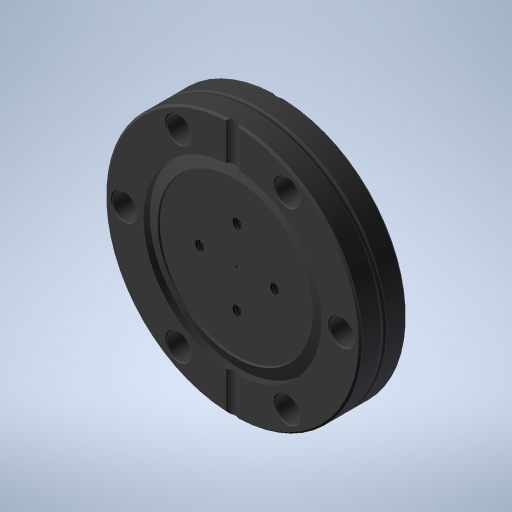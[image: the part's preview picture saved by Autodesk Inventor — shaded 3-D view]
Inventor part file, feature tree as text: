
AUTODESK INVENTOR PART (.ipt)
format: ipt  version: 2024 (Build 280153000, 153)  size: 361,472 bytes
history: native  units: in
note: dims shown in document units (in); Inventor stores cm internally (conversion verified against a paired STEP export)
features: hole x2, sketch x1
ambient origin geometry x8: Origin, YZ Plane, XZ Plane, XY Plane, X Axis, Y Axis, Z Axis, Center Point
bodies: Solid1 (feature_tree)
feature tree (3):
  sketch  "Sketch1"  dims[d0=0.4in d1=0.4in d2=0.4in d3=0.4in d4=0.104in d5=0.25in d6=0.279in d7=0.25in d8=0.5635in d9=0.25in d10=0.0in d11=0.04in d12=0.25in d13=0.375in d14=0.25in d15=0.5635in d16=0.25in d17=0.0in]
  hole  "Hole1"  [1 undecoded]
  hole  "Hole2"  [1 undecoded]
note: 2 required parameter values undecoded (feature->parameter linkage not recoverable at this tier; creation-order binding heuristic only, values carry confidence <= 0.55)
